# Revit family: SYSIMPLE FWM72A
name_source: partatom
category: Обобщенные модели
units: mm (PartAtom-declared; Revit-internal decimal feet)

## family parameters
Всегда вертикально = Да
Может служить основой для арматурных стержней = Нет
На основе рабочей плоскости = Нет
Общий = Нет
При загрузке вырезать с полостями = Нет
Размер круглого соединителя = Использовать диаметр
Тип детали = Нормальный
Точка расчета площади = Нет

## types (1)
- SYSIMPLE FWM72A
    Air guide size(mm) = /
    Body dimension(W) = 1100×330×235
    COP = /
    Capacity = /
    Chassis height（mm) = /
    Compressor quantity = /
    Compressor type = /
    Cooling Power input = /
    Cooling capacity = 7210/6129/4687
    Cooling current = /
    Current of Circuit breaker = /
    Design Pressure(Mpa） = 1.6
    EER = /
    Fan motor quantity = 1
    Front clearance(mm) = /
    Gross Weight = 23.0
    Heating capacity = 10807/9186/7025
    Heating current = /
    Heating power input = /
    Inlet/Outlet /Drain  Water Pipe = DN15
    Installation hole spacing（D) = /
    Installation hole spacing（W) = /
    Left Side clearance(ODU side mm) = /
    Left Side clearance(wall side mm) = 150
    Manufacturer = AUX
    Manufacturer URL = /
    Max.Current input = /
    Max.Power input = /
    Model = AFC-800WM/4B(L*)
    NET Weight = 20
    Noise Level(dB) = ≤49
    ODU fan ESP = /
    ODU fan type = /
    Operation range Heatling (°C） = /
    Operation range cooling (°C） = /
    Power = 220~240,50/60,1
    Product series = Wall Mounted FCU
    Protection grade = /
    Rear clearance(mm) = /
    Refrigerant Charged Volume(kg) = /
    Refrigerant type = /
    Right Side clearance(ODU side mm) = /
    Right Side clearance(wall side mm) = 150
    Top clearance(mm) = 150
